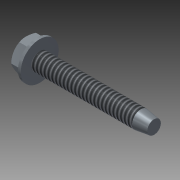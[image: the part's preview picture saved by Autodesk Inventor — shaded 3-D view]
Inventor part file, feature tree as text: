
AUTODESK INVENTOR PART (.ipt)
format: ipt  version: 2014 (Build 180170000, 170)  size: 167,424 bytes
history: native  units: mm (DEFAULTED — no unit token found)
features: sketch x4, extrude x2, other x1, chamfer x1, plane x1
ambient origin geometry x8: Origin, YZ Plane, XZ Plane, XY Plane, X Axis, Y Axis, Z Axis, Center Point
bodies: Solid1 (feature_tree), Body (feature_tree)
feature tree (9):
  extrude  "Head"  Depth=0.7874mm
  other  "IDS_WORKPLANE{1}"
  extrude  "Indent"  TaperAngle=90.0deg  [1 undecoded]
  chamfer  "Chamfer1"  [1 undecoded]
  plane  "Work Plane3"
  sketch  "Sketch1"  dims[d1=0.7874mm d2=4.826mm]
  sketch  "Sketch2"  dims[d3=31.75mm d77=90.0deg]
  sketch  "Sketch3"  dims[d6=31.75mm]
  sketch  "Sketch4"  dims[d7=0.0mm d10=0.0mm d11=7.9248mm d12=3.048mm d13=0.0mm d14=0.0mm d15=6.33984mm d16=0.3048mm d17=0.0mm d92=90.0deg d19=0.5334mm d20=3.7084mm d21=7.9248mm d22=10.5156mm d23=6.863078mm d98=45.0deg d99=0.0mm d100=0.0mm]
note: 2 required parameter values undecoded (feature->parameter linkage not recoverable at this tier; creation-order binding heuristic only, values carry confidence <= 0.55)
